# Revit family: RS400MK.60.x.150
name_source: partatom
category: Sanitärinstallationen
units: mm (PartAtom-declared; Revit-internal decimal feet)

## family parameters
Arbeitsebenenbasiert = Nein
Beim Laden mit Abzugskörper schneiden = Nein
Bemaßung runder Anschluss = Durchmesser verwenden
Gemeinsam genutzt = Nein
Immer vertikal = Ja
Raumberechnungspunkt = Nein
Teiletyp = Normal

## types (1)
- RS400MK.60.x.150
    Anschlusswert DU L/s = 0
    Baugruppenkennzeichen = D2030300
    Hersteller = Resitec
    Klebeblech mit Epoxidgrundierung = Ja
    RS_AVol-H = 170 mm  [stored 0.557743 ft]
    RS_AVol-L = 129 mm  [stored 0.423228 ft]
    RS_AVol-T = 129 mm  [stored 0.423228 ft]
    RS_DN1 = 60 mm  [stored 0.19685 ft]
    RS_DN1d = 65 mm  [stored 0.213255 ft]
    RS_DN2 = 0 mm  [stored 0 ft]
    RS_DVol-L = 300 mm  [stored 0.984252 ft]
    RS_DVol-T = 300 mm  [stored 0.984252 ft]
    RS_Manufacture = Resitec
    RS_URL = https://resitec.ch
    RS_dia001 = 138 mm  [stored 0.452756 ft]
    RS_dia002 = 110 mm  [stored 0.360892 ft]
    RS_dia10 = 114 mm  [stored 0.374016 ft]
    RS_diaRH1 = 150 mm  [stored 0.492126 ft]
    RS_dim001 = 75 mm  [stored 0.246063 ft]
    RS_dim002 = 125 mm  [stored 0.410105 ft]
    RS_dim003 = 80 mm  [stored 0.262467 ft]
    RS_dim10 = 250 mm  [stored 0.82021 ft]
    RS_s001 = 3 mm  [stored 0.00984252 ft]
    RS_s002 = 2 mm  [stored 0.00656168 ft]
    URL = https://www.resitec.ch
    Vorgabe-Ansicht = 0 mm  [stored 0 ft]

note: [stored X ft] marks values corroborated as IEEE doubles in the binary element streams (Revit-internal decimal feet)

## geometry (parser evidence)
native form markers: Blend x8
no freeform markers — native parametric forms only
